# Revit family: Water_Boiler-Navien-NFC-Condensing_Combi-NFC-H
name_source: partatom
category: Mechanical Equipment
units: mm (PartAtom-declared; Revit-internal decimal feet)

## family parameters
Cut with Voids When Loaded = No
Host = Face
OmniClass Number = 23.65.35.11
OmniClass Title = Supply Water Heaters
Part Type = Normal
Room Calculation Point = No
Round Connector Dimension = Use Diameter
Shared = No

## types (2) — shared parameters
2" Exhaust/Intake = Yes
3" Exhaust/Intake = No
Apparent Load = 0 VA
Assembly Code = D3010500
Auto Feeder Inlet = 1/2"
Certifications = Energy Star | AHRI | CSA | ASME | CSA Blue Star | CSA Blue Flame
Cold Water Inlet = 1"
Condensate Outlet = 1/2"
Default Elevation = 48"
Depth = 17 5/16"
Description = NFC-H Condensing Gas Hot Water Combination Boiler
Exhaust = 2"
Finish = Metal - Navien - White
Flow Rate = 0 GPM
Frequency = 60 Hz
Gas Connection Size = 1"
Gas Inlet = 1"
Heating Return = 1 1/4"
Heating Supply = 1 1/4"
Height = 33 1/2"
Hot Water Outlet = 1"
Ignition = Electronic ignition
Installation Type = Indoor Wall-Hung
Intake = 2"
Keynote = 22 33 00.A1
Manufacturer = Navien, Inc.
Manufacturer Fax Number = (949) 420-0430
Natural Gas Manifold Pressure = -0.03" to -0.92" WC
Natural Gas Supply Pressure = 3.5" to 10.5" WC
Number of Poles = 1
Phase = 1
Power Factor = 1
Product Documentation Link = https://www.navieninc.com
Product Name = NFC-H Series Combination Boilers
Product Page URL = https://www.navieninc.com
Propane Gas Manifold Pressure = -0.02" to -0.77" WC
Propane Gas Supply Pressure = 8.0" to 13.5" WC
URL = https://www.navieninc.com
Venting = Exhaust: 2 in or 3 in PVC, CPVC, Approved Polypropylene, Stainless Steel, 2 in or 3 in Special Gas Vent Type BH (Class III, A/B/C) | Intake: 2 in or 3 in PVC, CPVC, Polypropylene, Stainless Steel, ABS 2 in or 3 in Special Gas Vent Type BH (Class III, A/B/C) | Vent Clearance: 0 in to combustibles
Venting Type = Forced draft direct vent
Version = 2019 - v1.0.a
Voltage = 120 V
Warranty = https://www.navieninc.com
Warranty Note = Heat Exchangers: 10 years limited warranty (Residential), 5 years (Commercial) | Parts: 5 years (Residential), 3 years (Commercial)
Water Pressure = 12–80 psi
Weight = 141.00 lbf
Wi-Fi Ready = NaviLink Wi?Fi Control: This add-on accessory enables access to control temperatures remotely, access usage data and receive diagnostic notifications via smartphone or tablet.
Width = 17 5/16"

## per-type parameters (varying)
| type | Heating Capacity | Heating Capacity Note |
| NFC-250/175H | 175000.0 Btu/h | 13,300 to 175,000 BTUh |
| NFC-250/200H | 199900.0 Btu/h | 13,300 to 199,900 BTUh |

note: column(s) folded — value = type name in every type: Model

## geometry (parser evidence)
native form markers: Sweep x4
no freeform markers — native parametric forms only
